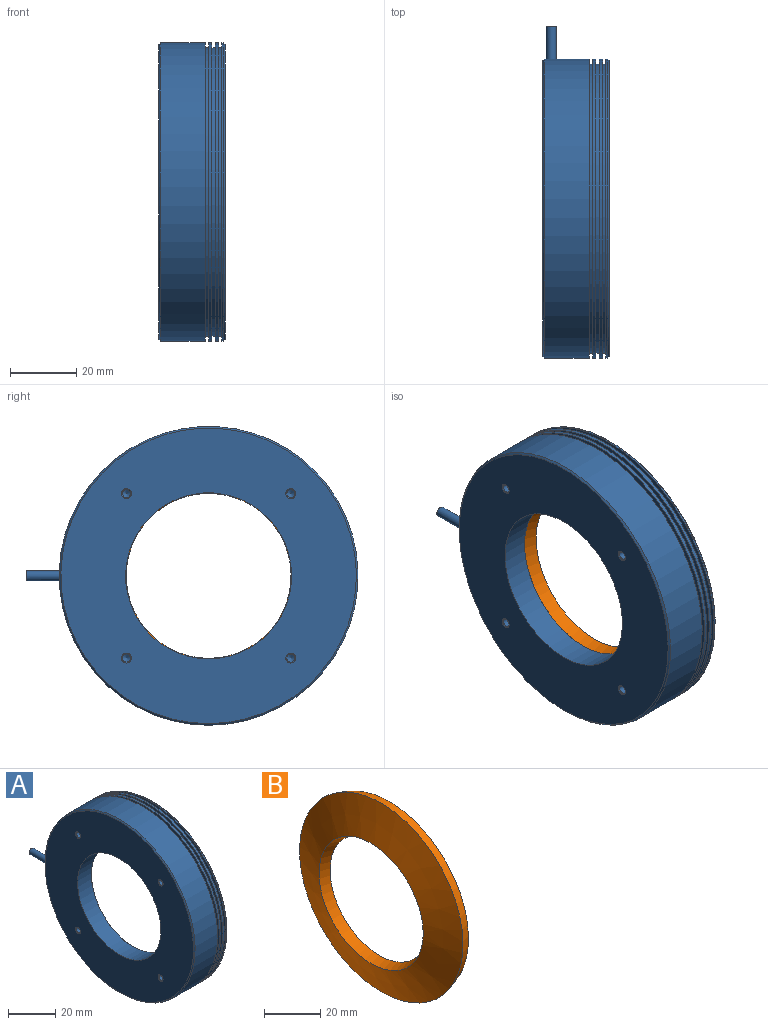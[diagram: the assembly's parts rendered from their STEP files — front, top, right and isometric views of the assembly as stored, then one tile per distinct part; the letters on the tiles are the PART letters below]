
ASSEMBLY  parts=2 mates=1
PART A: 37 faces, bbox 20x100x90 mm
  f0: cone r=1.23mm half-angle=60deg, axis (-1,0,0), area 5.5mm2, adj f34
  f1: plane 89x89mm, normal (-1,0,0), area 4229.4mm2, adj f2,f3,f24,f27,f30,f33
  f2: cylinder r=25mm len=50mm, axis (-1,0,0), area 1303.8mm2, adj f1,f23
  f3: cone r=45mm half-angle=45deg, axis (1,0,0), area 198.8mm2, adj f1,f4
  f4: cylinder r=45mm len=90mm, axis (-1,0,0), area 3810mm2, adj f3,f5,f36
  f5: plane 90x90mm, normal (1,0,0), area 417mm2, adj f4,f6
  f6: cylinder r=43.5mm len=87mm, axis (-1,0,0), area 273.3mm2, adj f5,f7
  f7: plane 90x90mm, normal (-1,0,0), area 417mm2, adj f6,f8
  f8: cylinder r=45mm len=90mm, axis (-1,0,0), area 282.7mm2, adj f7,f9
  f9: plane 90x90mm, normal (1,0,0), area 417mm2, adj f8,f10
  f10: cylinder r=43.5mm len=87mm, axis (-1,0,0), area 273.3mm2, adj f9,f11
  f11: plane 90x90mm, normal (-1,0,0), area 417mm2, adj f10,f12
  f12: cylinder r=45mm len=90mm, axis (-1,0,0), area 282.7mm2, adj f11,f13
  f13: plane 90x90mm, normal (1,0,0), area 417mm2, adj f12,f14
  f14: cylinder r=43.5mm len=87mm, axis (-1,0,0), area 273.3mm2, adj f13,f15
  f15: plane 90x90mm, normal (-1,0,0), area 417mm2, adj f14,f16
  f16: cylinder r=45mm len=90mm, axis (-1,0,0), area 141.4mm2, adj f15,f17
  f17: cone r=44.5mm half-angle=45deg, axis (-1,0,0), area 198.8mm2, adj f16,f18
  f18: plane 89x89mm, normal (1,0,0), area 758.3mm2, adj f17,f19
  f19: cylinder r=41.7mm len=83.4mm, axis (-1,0,0), area 1441mm2, adj f18,f20
  f20: plane 85x85mm, normal (-1,0,0), area 211.6mm2, adj f19,f21
  f21: cone r=25.32mm half-angle=71deg, axis (1,0,0), area 3871.7mm2, adj f20,f22
  f22: cone r=25.42mm half-angle=19deg, axis (-1,0,0), area 47.8mm2, adj f21,f23
  f23: plane 50.83x50.83mm, normal (1,0,0), area 65.8mm2, adj f2,f22
  f24: cone r=1.5mm half-angle=45deg, axis (-1,0,0), area 3.3mm2, adj f1,f25
  f25: cylinder r=1.23mm len=5.02mm, axis (-1,0,0), area 38.8mm2, adj f24,f26
  f26: cone r=1.23mm half-angle=60deg, axis (-1,0,0), area 5.5mm2, adj f25
  f27: cone r=1.5mm half-angle=45deg, axis (-1,0,0), area 3.3mm2, adj f1,f28
  f28: cylinder r=1.23mm len=5.02mm, axis (-1,0,0), area 38.8mm2, adj f27,f29
  f29: cone r=1.23mm half-angle=60deg, axis (-1,0,0), area 5.5mm2, adj f28
  f30: cone r=1.5mm half-angle=45deg, axis (-1,0,0), area 3.3mm2, adj f1,f31
  f31: cylinder r=1.23mm len=5.02mm, axis (-1,0,0), area 38.8mm2, adj f30,f32
  f32: cone r=1.23mm half-angle=60deg, axis (-1,0,0), area 5.5mm2, adj f31
  f33: cone r=1.5mm half-angle=45deg, axis (-1,0,0), area 3.3mm2, adj f1,f34
  f34: cylinder r=1.23mm len=5.02mm, axis (-1,0,0), area 38.8mm2, adj f0,f33
  f35: plane 3x3mm, normal (0,1,0), area 7.1mm2, adj f36
  f36: cylinder r=1.5mm len=10.03mm, axis (0,1,0), area 94.5mm2, adj f4,f35
PART B: 4 faces, bbox 9.3x82.4x82.4 mm
  f0: cone r=41.2mm half-angle=71deg, axis (1,0,0), area 3348.8mm2, adj f1,f3
  f1: cone r=26.26mm half-angle=19deg, axis (-1,0,0), area 706.3mm2, adj f0,f2
  f2: cone r=24.83mm half-angle=71deg, axis (1,0,0), area 3206.6mm2, adj f1,f3
  f3: cone r=39.77mm half-angle=19deg, axis (-1,0,0), area 1119.3mm2, adj f0,f2
PLACE A at identity fixed
PLACE B at identity
MATE fastened B.f0 <-> A.f2  axis (1,0,0) through (15.64,0,0)mm
